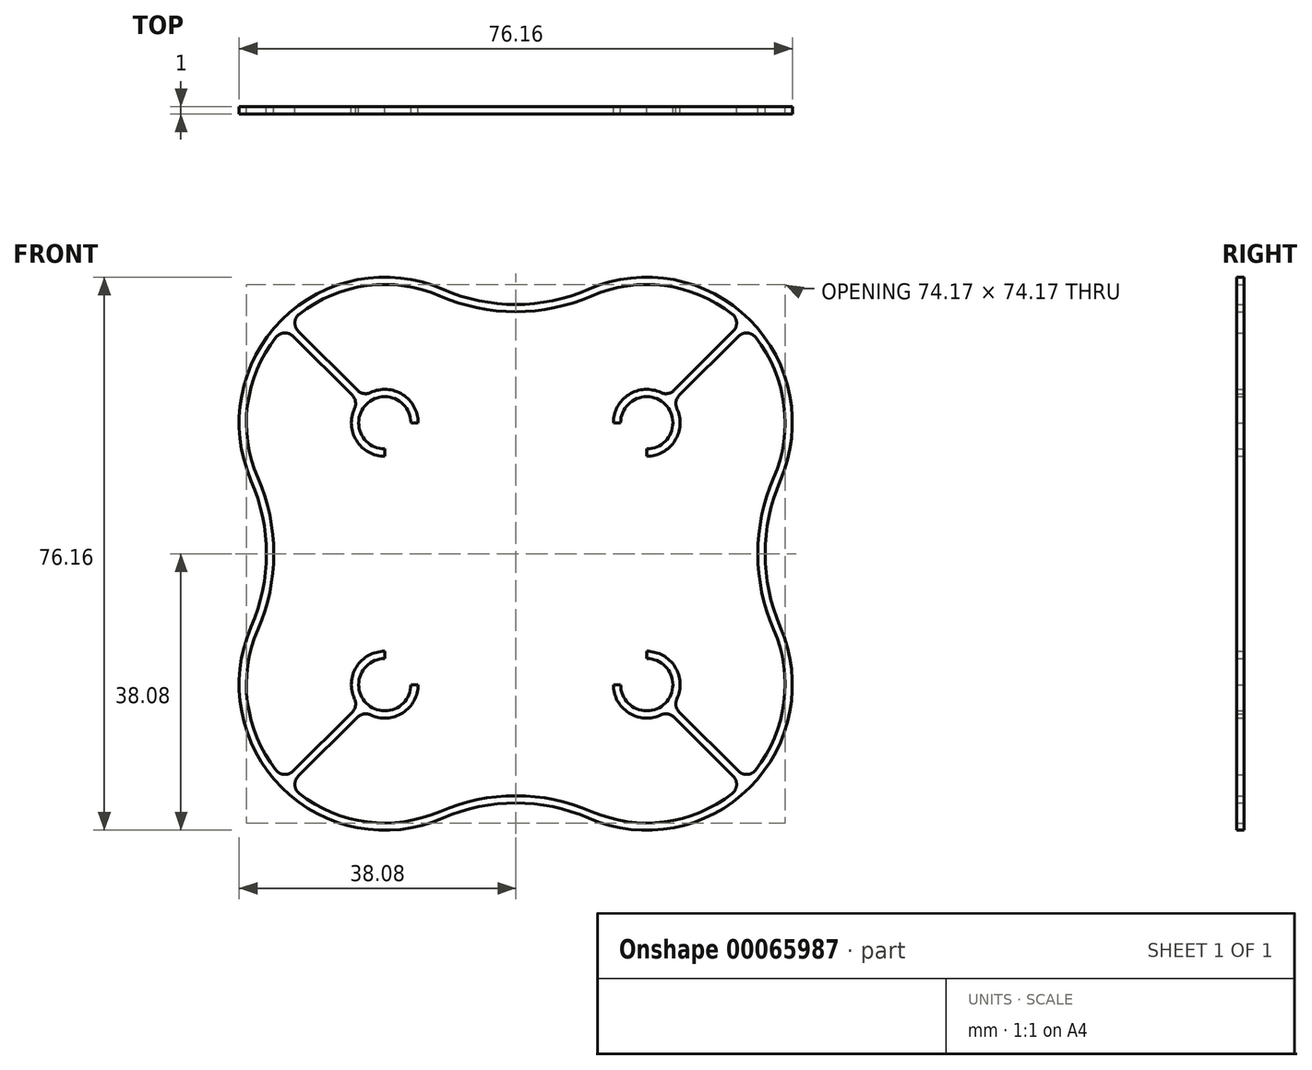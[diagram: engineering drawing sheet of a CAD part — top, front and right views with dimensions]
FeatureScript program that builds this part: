
annotation { "Feature Type Name" : "Feature", "Feature Type Description" : "" }
export const myFeature = defineFeature(function(context is Context, id is Id, definition is map)
    precondition{}
    {
        {
            var Q0;
            Q0=qCreatedBy(makeId("Front.planeOp"),FACE);
            var sketch = newSketch(context, id + "F0", { "sketchPlane" : qUnion([Q0])});
            skArc(sketch, "E0", {"start": v(-14.43, 18.03) * mm, "mid": v(-20.58, 20.58) * mm, "end": v(-18.03, 14.43) * mm});
            skLineSegment(sketch, "E1", {"start": v(-18.03, 18.03) * mm, "end": v(-20.58, 20.58) * mm, "construction": true});
            skLineSegment(sketch, "E2", {"start": v(-20.58, 20.58) * mm, "end": v(-31.5, 31.5) * mm, "construction": true});
            skArc(sketch, "E3", {"start": v(-35.5, 10.43) * mm, "mid": v(-36.8, 21.34) * mm, "end": v(-31.85, 31.15) * mm});
            skLineSegment(sketch, "E4", {"start": v(-18.03, 0) * mm, "end": v(-18.03, 18.03) * mm, "construction": true});
            skLineSegment(sketch, "E5", {"start": v(0, 18.03) * mm, "end": v(-18.03, 18.03) * mm, "construction": true});
            skArc(sketch, "E6", {"start": v(-35.5, 10.43) * mm, "mid": v(-33.88, 5.33) * mm, "end": v(-33.33, 0) * mm});
            skArc(sketch, "E7", {"start": v(-10.43, 35.5) * mm, "mid": v(-5.33, 33.88) * mm, "end": v(0, 33.33) * mm});
            skArc(sketch, "E8.0", {"start": v(-13.43, 18.03) * mm, "mid": v(-16.04, 22.18) * mm, "end": v(-20.91, 21.62) * mm});
            skLineSegment(sketch, "E9", {"start": v(-18.03, 13.43) * mm, "end": v(-18.03, 14.43) * mm});
            skLineSegment(sketch, "E10", {"start": v(-14.43, 18.03) * mm, "end": v(-13.43, 18.03) * mm});
            skArc(sketch, "E11.0", {"start": v(-10.03, 36.42) * mm, "mid": v(-5.12, 34.86) * mm, "end": v(0, 34.33) * mm});
            skArc(sketch, "E11.1", {"start": v(-36.42, 10.03) * mm, "mid": v(-32.21, 32.21) * mm, "end": v(-10.03, 36.42) * mm});
            skArc(sketch, "E11.2", {"start": v(-36.42, 10.03) * mm, "mid": v(-34.86, 5.12) * mm, "end": v(-34.33, 0) * mm});
            skLineSegment(sketch, "E12.0", {"start": v(-20.91, 21.62) * mm, "end": v(-31.15, 31.85) * mm});
            skLineSegment(sketch, "E13.0", {"start": v(-21.62, 20.91) * mm, "end": v(-31.85, 31.15) * mm});
            skArc(sketch, "E14.trimOffspring", {"start": v(-31.15, 31.85) * mm, "mid": v(-21.34, 36.8) * mm, "end": v(-10.43, 35.5) * mm});
            skArc(sketch, "E15.trimOffspring", {"start": v(-21.62, 20.91) * mm, "mid": v(-22.18, 16.04) * mm, "end": v(-18.03, 13.43) * mm});
            skLineSegment(sketch, "E16", {"start": v(0, 34.33) * mm, "end": v(0, 33.33) * mm});
            skLineSegment(sketch, "E17", {"start": v(-34.33, 0) * mm, "end": v(-33.33, 0) * mm});
            skSolve(sketch);
        }
        {
            var Q0;
            Q0 = qSketchRegion(id + "F0", true);
            extrude(context, id + "F1", {"entities" : qUnion([Q0]), "depth" : 1 * mm});
        }
        {
            var Q0;
            Q0=makeQuery(id+"F1.opExtrude","SWEPT_EDGE",EDGE,{"disambiguationData":[OSD([sQuery(id+"F0.wireOp",EDGE,"E3"),sQuery(id+"F0.wireOp",EDGE,"E13.0")])]});
            var Q1;
            Q1=makeQuery(id+"F1.opExtrude","SWEPT_EDGE",EDGE,{"disambiguationData":[OSD([sQuery(id+"F0.wireOp",EDGE,"E12.0"),sQuery(id+"F0.wireOp",EDGE,"E14.trimOffspring")])]});
            var Q2;
            Q2=makeQuery(id+"F1.opExtrude","SWEPT_EDGE",EDGE,{"disambiguationData":[OSD([sQuery(id+"F0.wireOp",EDGE,"E8.0"),sQuery(id+"F0.wireOp",EDGE,"E12.0")])]});
            var Q3;
            Q3=makeQuery(id+"F1.opExtrude","SWEPT_EDGE",EDGE,{"disambiguationData":[OSD([sQuery(id+"F0.wireOp",EDGE,"E13.0"),sQuery(id+"F0.wireOp",EDGE,"E15.trimOffspring")])]});
            fillet(context, id + "F2", {"entities" : qUnion([Q0, Q1, Q2, Q3]), "radius" : 1.59 * mm, "tangentPropagation" : true, "allowEdgeOverflow" : false});
        }
        {
            var Q0;
            Q0=makeQuery(id+"F1.opExtrude","SWEPT_BODY",BODY,{"disambiguationData":[OSD([sQuery(id+"F0.wireOp",EDGE,"E0"),sQuery(id+"F0.wireOp",EDGE,"E3"),sQuery(id+"F0.wireOp",EDGE,"E6"),sQuery(id+"F0.wireOp",EDGE,"E7"),sQuery(id+"F0.wireOp",EDGE,"E8.0"),sQuery(id+"F0.wireOp",EDGE,"E9"),sQuery(id+"F0.wireOp",EDGE,"E10"),sQuery(id+"F0.wireOp",EDGE,"E11.0"),sQuery(id+"F0.wireOp",EDGE,"E11.1"),sQuery(id+"F0.wireOp",EDGE,"E11.2"),sQuery(id+"F0.wireOp",EDGE,"E12.0"),sQuery(id+"F0.wireOp",EDGE,"E13.0"),sQuery(id+"F0.wireOp",EDGE,"E14.trimOffspring"),sQuery(id+"F0.wireOp",EDGE,"E15.trimOffspring"),sQuery(id+"F0.wireOp",EDGE,"E16"),sQuery(id+"F0.wireOp",EDGE,"E17")])]});
            var Q1;
            Q1=qCreatedBy(makeId("Top.planeOp"),FACE);
            mirror(context, id + "F3", {"operationType" : NewBodyOperationType.ADD, "entities" : qUnion([Q0]), "mirrorPlane" : qUnion([Q1])});
        }
        {
            var Q0;
            Q0=makeQuery(id+"F1.opExtrude","SWEPT_BODY",BODY,{"disambiguationData":[OSD([sQuery(id+"F0.wireOp",EDGE,"E0"),sQuery(id+"F0.wireOp",EDGE,"E3"),sQuery(id+"F0.wireOp",EDGE,"E6"),sQuery(id+"F0.wireOp",EDGE,"E7"),sQuery(id+"F0.wireOp",EDGE,"E8.0"),sQuery(id+"F0.wireOp",EDGE,"E9"),sQuery(id+"F0.wireOp",EDGE,"E10"),sQuery(id+"F0.wireOp",EDGE,"E11.0"),sQuery(id+"F0.wireOp",EDGE,"E11.1"),sQuery(id+"F0.wireOp",EDGE,"E11.2"),sQuery(id+"F0.wireOp",EDGE,"E12.0"),sQuery(id+"F0.wireOp",EDGE,"E13.0"),sQuery(id+"F0.wireOp",EDGE,"E14.trimOffspring"),sQuery(id+"F0.wireOp",EDGE,"E15.trimOffspring"),sQuery(id+"F0.wireOp",EDGE,"E16"),sQuery(id+"F0.wireOp",EDGE,"E17")])]});
            var Q1;
            Q1=qCreatedBy(makeId("Right.planeOp"),FACE);
            mirror(context, id + "F4", {"operationType" : NewBodyOperationType.ADD, "entities" : qUnion([Q0]), "mirrorPlane" : qUnion([Q1])});
        }
    });
